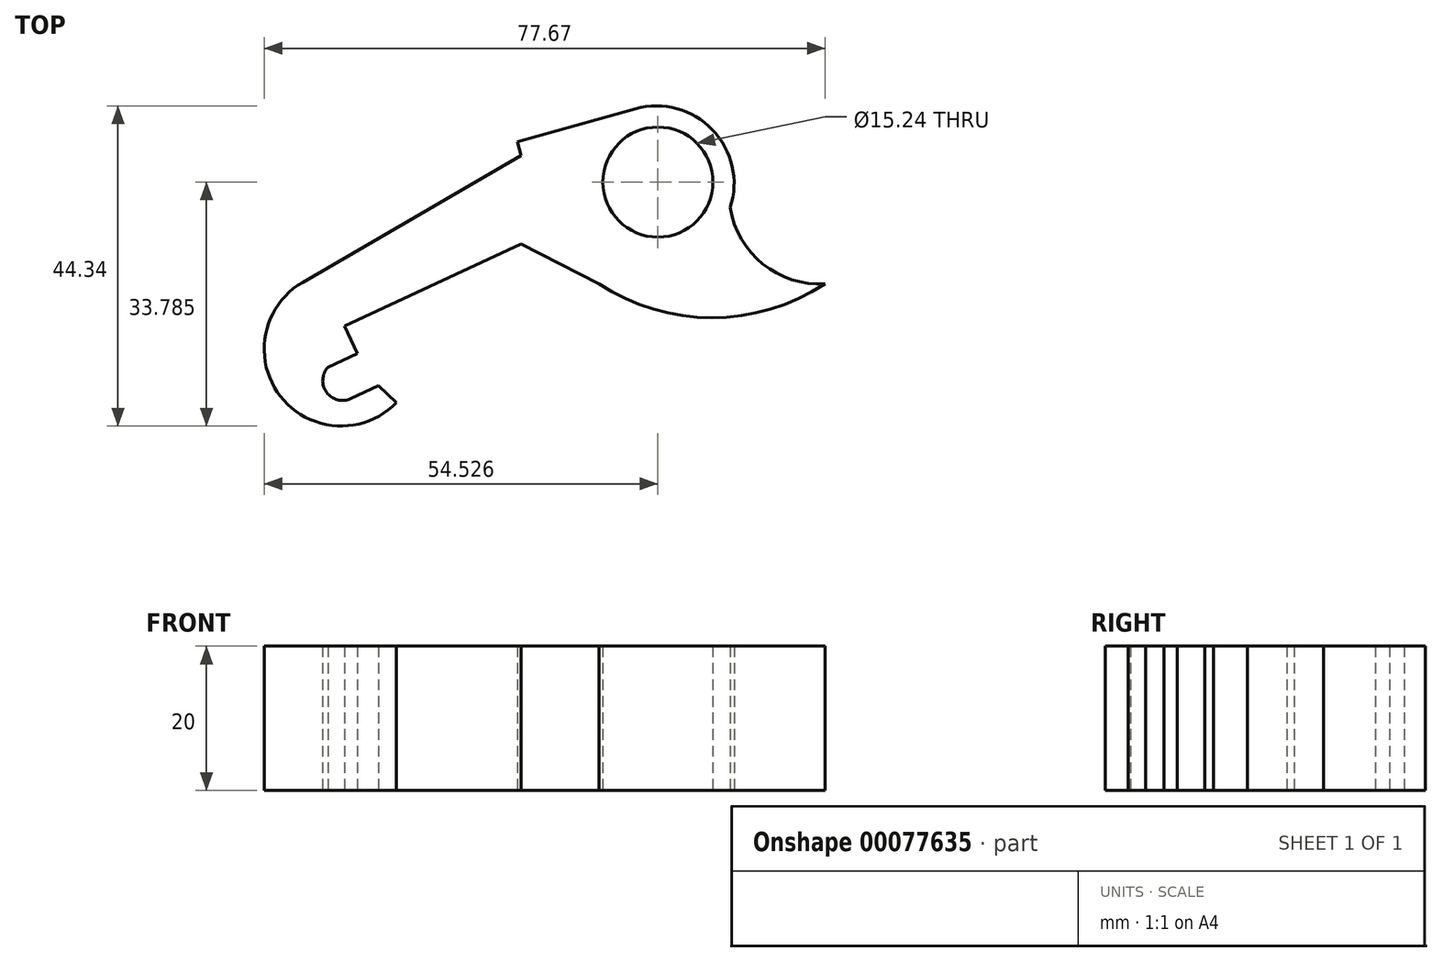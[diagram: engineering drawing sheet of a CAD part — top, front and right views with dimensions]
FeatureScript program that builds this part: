
annotation { "Feature Type Name" : "Feature", "Feature Type Description" : "" }
export const myFeature = defineFeature(function(context is Context, id is Id, definition is map)
    precondition{}
    {
        {
            var Q0;
            Q0=qCreatedBy(makeId("Top.planeOp"),FACE);
            var sketch = newSketch(context, id + "F0", { "sketchPlane" : qUnion([Q0])});
            skLineSegment(sketch, "E0", {"start": v(-20.42, 12.93) * mm, "end": v(9.86, 30.48) * mm});
            skLineSegment(sketch, "E1", {"start": v(9.86, 30.48) * mm, "end": v(9.32, 32.4) * mm});
            skLineSegment(sketch, "E2", {"start": v(9.32, 32.4) * mm, "end": v(25.7, 36.98) * mm});
            skCircle(sketch, "E3", {"center": v(28.79, 26.82) * mm, "radius": 7.62 * mm});
            skCircle(sketch, "E4", {"center": v(28.79, 26.82) * mm, "radius": 10.62 * mm, "construction": true});
            skArc(sketch, "E5", {"start": v(38.8, 23.31) * mm, "mid": v(36.34, 34.08) * mm, "end": v(25.7, 36.98) * mm});
            skArc(sketch, "E6", {"start": v(38.8, 23.31) * mm, "mid": v(43.32, 15.49) * mm, "end": v(51.93, 12.74) * mm});
            skArc(sketch, "E7", {"start": v(20.6, 12.74) * mm, "mid": v(36.27, 8.04) * mm, "end": v(51.93, 12.74) * mm});
            skArc(sketch, "E8", {"start": v(-20.42, 12.93) * mm, "mid": v(-23.5, -2.85) * mm, "end": v(-7.44, -3.74) * mm});
            skLineSegment(sketch, "E9", {"start": v(-7.44, -3.74) * mm, "end": v(-9.91, -1.38) * mm});
            skLineSegment(sketch, "E10", {"start": v(20.6, 12.74) * mm, "end": v(9.81, 18.24) * mm});
            skLineSegment(sketch, "E11", {"start": v(9.81, 18.24) * mm, "end": v(-14.63, 6.87) * mm});
            skLineSegment(sketch, "E12", {"start": v(-14.63, 6.87) * mm, "end": v(-12.85, 3.05) * mm});
            skLineSegment(sketch, "E13", {"start": v(-12.85, 3.05) * mm, "end": v(-16.91, 1.16) * mm});
            skLineSegment(sketch, "E14", {"start": v(-9.91, -1.38) * mm, "end": v(-13.74, -3.16) * mm});
            skPoint(sketch, "E14.endSnap0", {"position": v(-13.74, 4.96) * mm});
            skArc(sketch, "E15", {"start": v(-16.91, 1.16) * mm, "mid": v(-17.1, -2.3) * mm, "end": v(-13.74, -3.16) * mm});
            skSolve(sketch);
        }
        {
            var Q0;
            Q0=makeQuery(id+"F0.imprint","IMPRINT",FACE,{"disambiguationData":[TD([[makeQuery(id+"F0.imprint","IMPRINT",EDGE,{"derivedFrom":sQuery(id+"F0.wireOp",EDGE,"E0")}),-1.0]])]});
            extrude(context, id + "F1", {"entities" : qUnion([Q0]), "depth" : 20 * mm});
        }
    });
